# Revit family: RBA4090-346
name_source: partatom
category: Plumbing Fixtures
units: mm (PartAtom-declared; Revit-internal decimal feet)

## family parameters
Always vertical = No
Cut with Voids When Loaded = No
Part Type = Normal
Room Calculation Point = No
Round Connector Dimension = Use Diameter
Shared = No
Work Plane-Based = No

## types (1)
- RBA4090-346
    BAR = Stainless Steel, Satin Finish
    Default Elevation = 0 mm  [stored 0 ft]
    Description = 90° WC Grab Rail Set - Right Hand, 450 Straight
    Distance Away from Toilet = 1090 mm  [stored 3.57612 ft]
    Distance Away from Wall = 100 mm  [stored 0.328084 ft]
    Manufacturer = RBA Group
    Model = RBA4090-346
    Modified Issue = 20170620
    OFFSET = 800 mm  [stored 2.62467 ft]
    URL = http://www.rba.com.au

note: [stored X ft] marks values corroborated as IEEE doubles in the binary element streams (Revit-internal decimal feet)

## geometry (parser evidence)
native form markers: Blend x8, Sweep x7
no freeform markers — native parametric forms only
